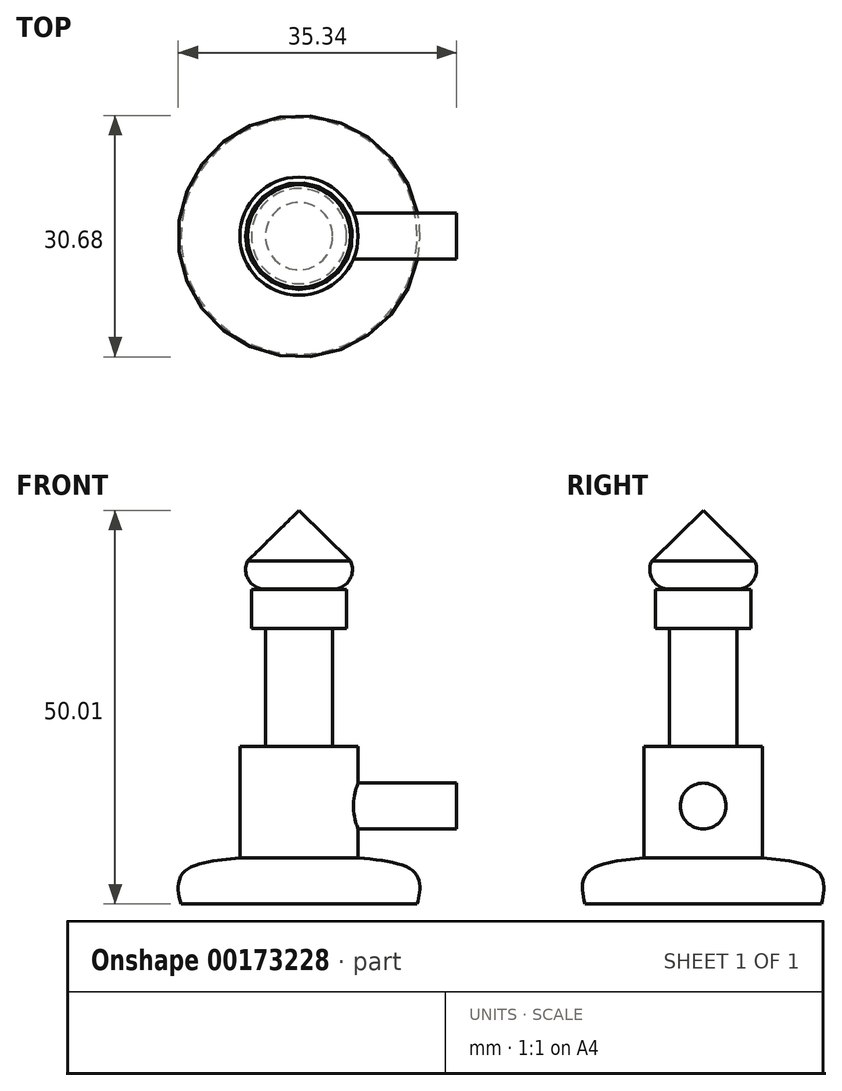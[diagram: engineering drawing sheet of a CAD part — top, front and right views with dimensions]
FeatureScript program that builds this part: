
annotation { "Feature Type Name" : "Feature", "Feature Type Description" : "" }
export const myFeature = defineFeature(function(context is Context, id is Id, definition is map)
    precondition{}
    {
        {
            var Q0;
            Q0=qCreatedBy(makeId("Front.planeOp"),FACE);
            var sketch = newSketch(context, id + "F0", { "sketchPlane" : qUnion([Q0])});
            skFitSpline(sketch, "E0", {"points": [v(-15, 0) * mm, v(-14.24, 4.4) * mm, v(0, 8.12) * mm, v(-1.3, 15.03) * mm], "startDerivative": vector(-4.6, 16.78) * mm, "endDerivative": vector(-13.27, 12.66) * mm});
            skLineSegment(sketch, "E1", {"start": v(0, 13.08) * mm, "end": v(0, 0) * mm});
            skPoint(sketch, "E2.orphan", {"position": v(0, 33.42) * mm});
            skLineSegment(sketch, "E3", {"start": v(0, 8.12) * mm, "end": v(0, 0) * mm});
            skLineSegment(sketch, "E4", {"start": v(0, 0) * mm, "end": v(-15, 0) * mm});
            skSolve(sketch);
        }
        {
            var Q0;
            Q0=makeQuery(id+"F0.imprint","IMPRINT",FACE,{"disambiguationData":[TD([[makeQuery(id+"F0.imprint","IMPRINT",EDGE,{"derivedFrom":sQuery(id+"F0.wireOp",EDGE,"E0")}),-1.0]])]});
            var Q1;
            Q1=sQuery(id+"F0.wireOp",EDGE,"E3");
            revolve(context, id + "F1", {"entities" : qUnion([Q0]), "axis" : qUnion([Q1]), "revolveType" : RevolveType.FULL});
        }
        {
            var Q0;
            Q0=qCreatedBy(makeId("Top.planeOp"),FACE);
            var sketch = newSketch(context, id + "F2", { "sketchPlane" : qUnion([Q0])});
            skCircle(sketch, "E5", {"center": v(0, 0) * mm, "radius": 7.5 * mm});
            skSolve(sketch);
        }
        {
            var Q0;
            Q0 = qSketchRegion(id + "F2", true);
            extrude(context, id + "F3", {"entities" : qUnion([Q0]), "operationType" : NewBodyOperationType.ADD, "depth" : 20 * mm});
        }
        {
            var Q0;
            Q0=makeQuery(id+"F3.opExtrude","CAP_FACE",FACE,{"disambiguationData":[OSD([sQuery(id+"F2.wireOp",EDGE,"E5")])],"isStart":false});
            var sketch = newSketch(context, id + "F4", { "sketchPlane" : qUnion([Q0])});
            skCircle(sketch, "E6", {"center": v(0, 0) * mm, "radius": 4.28 * mm});
            skSolve(sketch);
        }
        {
            var Q0;
            Q0=makeQuery(id+"F4.imprint","IMPRINT",FACE,{"disambiguationData":[TD([[makeQuery(id+"F4.imprint","IMPRINT",EDGE,{"derivedFrom":sQuery(id+"F4.wireOp",EDGE,"E6")}),1.0]])]});
            var Q1;
            Q1 = qSketchRegion(id + "F6", true);
            extrude(context, id + "F5", {"entities" : qUnion([Q0, Q1]), "operationType" : NewBodyOperationType.ADD, "depth" : 15 * mm});
        }
        {
            var Q0;
            Q0=qCreatedBy(makeId("Right.planeOp"),FACE);
            var sketch = newSketch(context, id + "F6", { "sketchPlane" : qUnion([Q0])});
            skCircle(sketch, "E7", {"center": v(0, 12.45) * mm, "radius": 2.91 * mm});
            skSolve(sketch);
        }
        {
            var Q0;
            Q0 = qSketchRegion(id + "F6", true);
            extrude(context, id + "F7", {"entities" : qUnion([Q0]), "operationType" : NewBodyOperationType.ADD, "depth" : 20 * mm});
        }
        {
            var Q0;
            Q0=makeQuery(id+"F5.opExtrude","CAP_FACE",FACE,{"disambiguationData":[OSD([sQuery(id+"F4.wireOp",EDGE,"E6")])],"isStart":false});
            var sketch = newSketch(context, id + "F8", { "sketchPlane" : qUnion([Q0])});
            skCircle(sketch, "E8", {"center": v(0, 0) * mm, "radius": 6.05 * mm});
            skSolve(sketch);
        }
        {
            var Q0;
            Q0 = qSketchRegion(id + "F8", true);
            extrude(context, id + "F9", {"entities" : qUnion([Q0]), "operationType" : NewBodyOperationType.ADD, "depth" : 5 * mm});
        }
        {
            var Q0;
            Q0=qCreatedBy(makeId("Front.planeOp"),FACE);
            var sketch = newSketch(context, id + "F10", { "sketchPlane" : qUnion([Q0])});
            skLineSegment(sketch, "E9", {"start": v(0, 40) * mm, "end": v(0, 50) * mm});
            skLineSegment(sketch, "E10", {"start": v(0, 40) * mm, "end": v(-4.3, 40) * mm});
            skArc(sketch, "E11", {"start": v(-6.52, 43.6) * mm, "mid": v(-6.41, 41.18) * mm, "end": v(-4.3, 40) * mm});
            skLineSegment(sketch, "E12", {"start": v(-6.52, 43.6) * mm, "end": v(0, 50) * mm});
            skSolve(sketch);
        }
        {
            var Q0;
            Q0=makeQuery(id+"F10.imprint","IMPRINT",FACE,{"disambiguationData":[TD([[makeQuery(id+"F10.imprint","IMPRINT",EDGE,{"derivedFrom":sQuery(id+"F10.wireOp",EDGE,"E9")}),1.0]])]});
            var Q1;
            Q1=sQuery(id+"F10.wireOp",EDGE,"E9");
            revolve(context, id + "F11", {"operationType" : NewBodyOperationType.ADD, "entities" : qUnion([Q0]), "axis" : qUnion([Q1]), "revolveType" : RevolveType.FULL});
        }
    });
